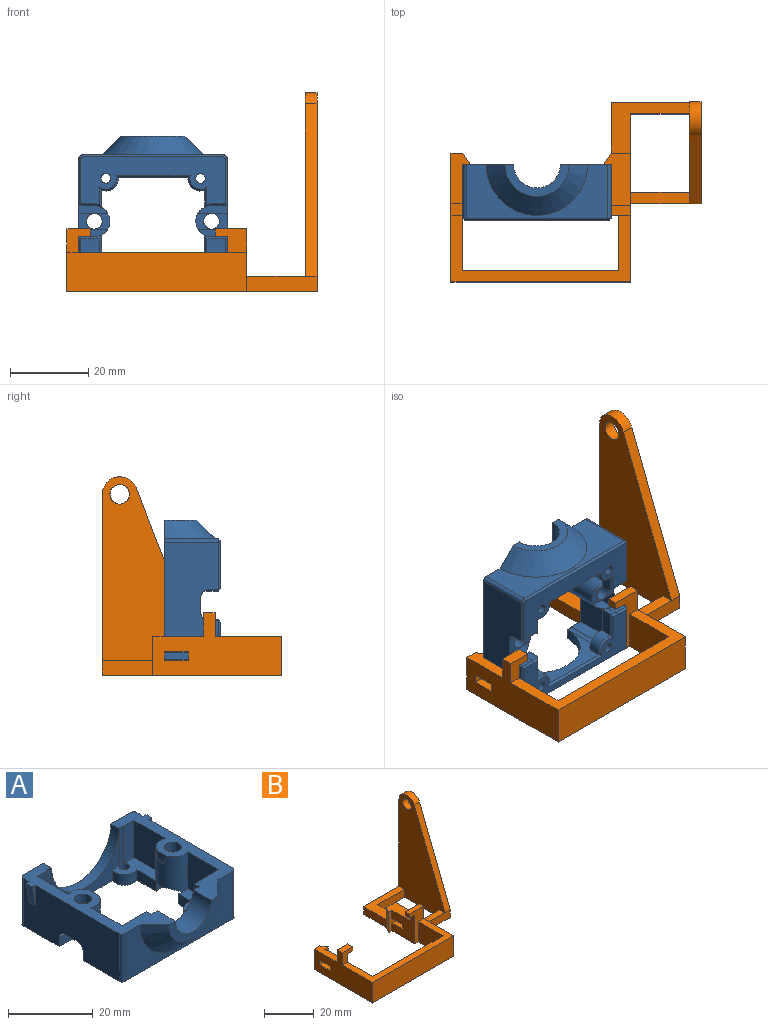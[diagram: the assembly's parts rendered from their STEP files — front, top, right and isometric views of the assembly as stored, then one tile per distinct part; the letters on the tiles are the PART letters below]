
ASSEMBLY  parts=2 mates=1
PART A: 100 faces, bbox 40.4x39.2x14.7 mm
  f0: cylinder r=2mm len=7.46mm, axis (1,0,0), area 18.6mm2, adj f8,f9,f10,f15,f16,f34,f89,f91
  f1: cylinder r=2mm len=7.46mm, axis (-1,0,0), area 18.6mm2, adj f4,f5,f11,f14,f17,f23,f86,f88
  f2: cylinder r=2mm len=7.46mm, axis (-1,0,0), area 18.6mm2, adj f7,f8,f10,f34,f36,f38,f89,f90
  f3: cylinder r=2mm len=7.46mm, axis (1,0,0), area 18.6mm2, adj f5,f6,f11,f23,f28,f32,f86,f87
  f4: cylinder r=4mm len=3mm, axis (0,0,-1), area 5.4mm2, adj f1,f14,f44,f88,f95
  f5: cylinder r=4mm len=10.75mm, axis (0,0,-1), area 143.3mm2, adj f1,f3,f14,f17,f27,f28,f32,f39
  f6: cylinder r=4mm len=3mm, axis (0,0,-1), area 5.4mm2, adj f3,f28,f45,f87,f93
  f7: cylinder r=4mm len=3mm, axis (0,0,-1), area 5.4mm2, adj f2,f38,f43,f90,f97
  f8: cylinder r=4mm len=10.75mm, axis (0,0,-1), area 143.3mm2, adj f0,f2,f10,f15,f16,f26,f36,f38
  f9: cylinder r=4mm len=3mm, axis (0,0,-1), area 5.4mm2, adj f0,f15,f42,f91,f99
  f10: plane 4x4mm, normal (0,0,-1), area 9mm2, adj f0,f2,f8,f19
  f11: plane 4x4mm, normal (0,0,-1), area 9.7mm2, adj f1,f3,f18,f23
  f12: plane 37.38x12.57mm, normal (0,0,-1), area 262.9mm2, adj f21,f51,f52,f53,f57,f58,f61,f63
  f13: plane 37.38x12.57mm, normal (0,0,-1), area 186.9mm2, adj f20,f54,f55,f56,f59,f60,f66,f68
  f14: plane 12.72x10.63mm, normal (0,0,1), area 67.5mm2, adj f1,f4,f5,f17,f29,f33,f41,f44
  f15: plane 10.63x7.24mm, normal (0,0,1), area 41.8mm2, adj f0,f8,f9,f16,f25,f31,f42,f67
  f16: plane 10.75x10.38mm, normal (1,0,0), area 111.6mm2, adj f0,f8,f15,f26,f31
  f17: plane 10.75x10.38mm, normal (-1,0,0), area 111.6mm2, adj f1,f5,f14,f27,f33
  f18: cylinder r=2mm len=9.25mm, axis (0,0,-1), area 116.2mm2, adj f11,f27,f86
  f19: cylinder r=2mm len=9.25mm, axis (0,0,-1), area 116.2mm2, adj f10,f26,f89
  f20: plane 12.28x0.52mm, normal (-0.71,0,-0.71), area 8.3mm2, adj f13,f34,f82,f83,f98
  f21: plane 12.28x0.52mm, normal (0.71,0,-0.71), area 8.3mm2, adj f12,f23,f80,f81,f94
  f22: plane 6x1mm, normal (0,1,0), area 3mm2, adj f23,f27,f73
  f23: plane 32x13.75mm, normal (1,0,0), area 393.7mm2, adj f1,f3,f11,f21,f22,f27,f59,f69
  f24: plane 10.75x3.35mm, normal (0,-1,0), area 36mm2, adj f27,f28,f32,f66
  f25: plane 22.63x13.75mm, normal (0,-1,0), area 96.8mm2, adj f15,f26,f28,f30,f56,f65,f66,f67
  f26: plane 38.8x14mm, normal (0,0,1), area 179mm2, adj f8,f16,f19,f25,f30,f31,f33,f34
  f27: plane 38.8x14mm, normal (0,0,1), area 179mm2, adj f5,f17,f18,f22,f23,f24,f30,f32
  f28: plane 10.63x7.41mm, normal (0,0,1), area 42.4mm2, adj f3,f5,f6,f24,f25,f32,f45,f65
  f29: cylinder r=11.3mm len=6.97mm, axis (0,1,0), area 21.2mm2, adj f14,f33,f38,f41
  f30: cylinder r=11.3mm len=22.6mm, axis (0,1,0), area 99.4mm2, adj f25,f26,f27,f37,f66
  f31: plane 10.75x3.18mm, normal (0,-1,0), area 34.2mm2, adj f15,f16,f26,f68
  f32: plane 10.75x10.38mm, normal (-1,0,0), area 111.6mm2, adj f3,f5,f24,f27,f28
  f33: plane 32.4x11.3mm, normal (0,1,0), area 250.3mm2, adj f14,f17,f26,f27,f29,f36,f38,f46
  f34: plane 32x13.75mm, normal (-1,0,0), area 393.7mm2, adj f0,f2,f20,f26,f58,f70,f71,f72
  f35: plane 36x13.75mm, normal (0,-1,0), area 229.5mm2, adj f26,f27,f50,f57,f78,f80
  f36: plane 10.75x10.38mm, normal (1,0,0), area 111.6mm2, adj f2,f8,f26,f33,f38
  f37: plane 36x13.75mm, normal (0,1,0), area 294.4mm2, adj f26,f27,f30,f60,f82,f84
  f38: plane 12.72x10.63mm, normal (0,0,1), area 68mm2, adj f2,f7,f8,f29,f33,f36,f41,f43
  f39: cylinder r=11.3mm len=3.04mm, axis (0,1,0), area 6.3mm2, adj f5,f27
  f40: cylinder r=11.3mm len=3.04mm, axis (0,1,0), area 6.3mm2, adj f8,f26
  f41: plane 17.76x3mm, normal (0,1,0), area 50.7mm2, adj f14,f29,f38,f51,f62,f64
  f42: plane 6.58x3mm, normal (1,0,0), area 19.7mm2, adj f9,f15,f55,f67
  f43: plane 4.39x3mm, normal (1,0,0), area 13.2mm2, adj f7,f38,f53,f62
  f44: plane 4.34x3mm, normal (-1,0,0), area 13mm2, adj f4,f14,f52,f64
  f45: plane 6.64x3mm, normal (-1,0,0), area 19.9mm2, adj f6,f28,f54,f65
  f46: cylinder r=8mm len=16mm, axis (0,1,0), area 40.2mm2, adj f26,f27,f33,f47
  f47: plane 16x8mm, normal (0,1,0), area 44mm2, adj f26,f27,f46,f48
  f48: cylinder r=6mm len=12mm, axis (0,1,0), area 113.1mm2, adj f26,f27,f47,f49
  f49: plane 16.4x8.2mm, normal (0,-1,0), area 49.1mm2, adj f26,f27,f48,f50
  f50: cone r=9mm half-angle=45deg, axis (0,1,0), area 226.1mm2, adj f26,f27,f35,f49
  f51: plane 18.98x0.54mm, normal (0,0.71,-0.71), area 13mm2, adj f12,f41,f74,f75
  f52: plane 5.19x0.57mm, normal (-0.71,0,-0.71), area 3.1mm2, adj f12,f44,f74,f95
  f53: plane 5.3x0.57mm, normal (0.71,0,-0.71), area 3.1mm2, adj f12,f43,f75,f97
  f54: plane 7.56x0.57mm, normal (-0.71,0,-0.71), area 4.7mm2, adj f13,f45,f77,f93
  f55: plane 7.43x0.56mm, normal (0.71,0,-0.71), area 4.6mm2, adj f13,f42,f76,f99
  f56: plane 19.64x0.56mm, normal (0,-0.71,-0.71), area 13.3mm2, adj f13,f25,f76,f77
  f57: plane 36.53x0.52mm, normal (0,-0.71,-0.71), area 25.5mm2, adj f12,f35,f78,f79,f80,f81
  f58: plane 12.28x0.52mm, normal (-0.71,0,-0.71), area 8.3mm2, adj f12,f34,f78,f79,f96
  f59: plane 12.28x0.52mm, normal (0.71,0,-0.71), area 8.3mm2, adj f13,f23,f84,f85,f92
  f60: plane 36.53x0.52mm, normal (0,0.71,-0.71), area 25.5mm2, adj f13,f37,f82,f83,f84,f85
  f61: cylinder r=1.25mm len=3.5mm, axis (0,0,-1), area 27.5mm2, adj f12,f38
  f62: cylinder r=3.25mm len=4.39mm, axis (0,0,-1), area 19.4mm2, adj f38,f41,f43,f75
  f63: cylinder r=1.25mm len=3.5mm, axis (0,0,-1), area 27.5mm2, adj f12,f14
  f64: cylinder r=3.25mm len=4.26mm, axis (0,0,-1), area 19mm2, adj f14,f41,f44,f74
  f65: cylinder r=3.25mm len=4.41mm, axis (0,0,-1), area 21.8mm2, adj f25,f28,f45,f77
  f66: cylinder r=1.25mm len=14.25mm, axis (0,0,-1), area 46.4mm2, adj f13,f24,f25,f27,f28,f30
  f67: cylinder r=3.25mm len=4.24mm, axis (0,0,-1), area 21.2mm2, adj f15,f25,f42,f76
  f68: cylinder r=1.25mm len=14.25mm, axis (0,0,-1), area 46.5mm2, adj f13,f15,f25,f26,f31
  f69: plane 6x1mm, normal (0,-1,0), area 3mm2, adj f23,f27,f73
  f70: plane 6x1mm, normal (0,-1,0), area 3mm2, adj f26,f34,f72
  f71: plane 6x1mm, normal (0,1,0), area 3mm2, adj f26,f34,f72
  f72: plane 6x2mm, normal (-0.99,0,-0.16), area 12.2mm2, adj f26,f34,f70,f71
  f73: plane 6x2mm, normal (0.99,0,-0.16), area 12.2mm2, adj f22,f23,f27,f69
  f74: cone r=2.75mm half-angle=45deg, axis (0,0,1), area 4.6mm2, adj f12,f51,f52,f64
  f75: cone r=2.75mm half-angle=45deg, axis (0,0,1), area 4.7mm2, adj f12,f51,f53,f62
  f76: cone r=2.75mm half-angle=45deg, axis (0,0,1), area 5.2mm2, adj f13,f55,f56,f67
  f77: cone r=2.75mm half-angle=45deg, axis (0,0,1), area 5.3mm2, adj f13,f54,f56,f65
  f78: cylinder r=1mm len=13.78mm, axis (0,0,-1), area 21.6mm2, adj f26,f34,f35,f57,f58,f79
  f79: cylinder r=1mm len=1.17mm, axis (-0.58,-0.58,0.58), area 0.8mm2, adj f12,f57,f58,f78
  f80: cylinder r=1mm len=13.78mm, axis (0,0,1), area 21.6mm2, adj f21,f23,f27,f35,f57,f81
  f81: cylinder r=1mm len=1.17mm, axis (0.58,-0.58,0.58), area 0.8mm2, adj f12,f21,f57,f80
  f82: cylinder r=1mm len=13.78mm, axis (0,0,1), area 21.6mm2, adj f20,f26,f34,f37,f60,f83
  f83: cylinder r=1mm len=1.17mm, axis (0.58,-0.58,-0.58), area 0.8mm2, adj f13,f20,f60,f82
  f84: cylinder r=1mm len=13.78mm, axis (0,0,-1), area 21.6mm2, adj f23,f27,f37,f59,f60,f85
  f85: cylinder r=1mm len=1.17mm, axis (-0.58,-0.58,-0.58), area 0.8mm2, adj f13,f59,f60,f84
  f86: plane 4x4mm, normal (0,0,-1), area 9mm2, adj f1,f3,f5,f18
  f87: plane 4x2.5mm, normal (0,-1,0), area 10mm2, adj f3,f6,f23,f92
  f88: plane 4x2.5mm, normal (0,1,0), area 10mm2, adj f1,f4,f23,f94
  f89: plane 4x4mm, normal (0,0,-1), area 9.7mm2, adj f0,f2,f19,f34
  f90: plane 4x2.5mm, normal (0,1,0), area 10mm2, adj f2,f7,f34,f96
  f91: plane 4x2.5mm, normal (0,-1,0), area 10mm2, adj f0,f9,f34,f98
  f92: plane 4x0.5mm, normal (0,-0.71,-0.71), area 2.7mm2, adj f13,f59,f87,f93
  f93: cone r=4mm half-angle=45deg, axis (0,0,-1), area 1.1mm2, adj f6,f13,f54,f92
  f94: plane 4x0.5mm, normal (0,0.71,-0.71), area 2.7mm2, adj f12,f21,f88,f95
  f95: cone r=4mm half-angle=45deg, axis (0,0,-1), area 1.1mm2, adj f4,f12,f52,f94
  f96: plane 4x0.5mm, normal (0,0.71,-0.71), area 2.7mm2, adj f12,f58,f90,f97
  f97: cone r=4mm half-angle=45deg, axis (0,0,-1), area 1.1mm2, adj f7,f12,f53,f96
  f98: plane 4x0.5mm, normal (0,-0.71,-0.71), area 2.7mm2, adj f13,f20,f91,f99
  f99: cone r=4mm half-angle=45deg, axis (0,0,-1), area 1.1mm2, adj f9,f13,f55,f98
PART B: 45 faces, bbox 64x46x50.8 mm
  f0: plane 50.8x26mm, normal (1,0,0), area 862mm2, adj f33,f37,f38,f42,f43,f44
  f1: plane 15x3mm, normal (0,0,1), area 45mm2, adj f3,f38,f40,f41
  f2: plane 6.2x5mm, normal (0,1,0), area 31mm2, adj f3,f23,f27,f36
  f3: plane 43x16mm, normal (1,0,0), area 358.4mm2, adj f1,f2,f6,f7,f9,f10,f19,f20
  f4: plane 3x2.5mm, normal (0,0,-1), area 7.5mm2, adj f5,f7,f8,f9
  f5: plane 2.5x2mm, normal (-1,0,0), area 5mm2, adj f4,f6,f7,f9
  f6: plane 8x2.5mm, normal (0,0,1), area 20mm2, adj f3,f5,f7,f9
  f7: plane 16x8mm, normal (0,-1,0), area 56mm2, adj f3,f4,f5,f6,f8,f10,f33,f34
  f8: plane 14x12.91mm, normal (-1,0,0), area 125.9mm2, adj f4,f7,f9,f20,f21,f22,f23,f28
  f9: plane 8x6mm, normal (0,1,0), area 36mm2, adj f3,f4,f5,f6,f8,f23
  f10: plane 46x17.09mm, normal (0,0,1), area 222.5mm2, adj f3,f7,f14,f15,f16,f19,f32,f34
  f11: plane 3x2mm, normal (1,0,0), area 6mm2, adj f12,f13,f15,f17
  f12: plane 3x3mm, normal (0,0,-1), area 9mm2, adj f11,f15,f16,f17
  f13: plane 6x3mm, normal (0,0,1), area 18mm2, adj f11,f14,f15,f17
  f14: plane 33x16mm, normal (-1,0,0), area 334.8mm2, adj f10,f13,f15,f17,f18,f19,f24,f25
  f15: plane 6x6mm, normal (0,-1,0), area 24mm2, adj f10,f11,f12,f13,f14,f16
  f16: plane 27x14mm, normal (1,0,0), area 268.8mm2, adj f10,f12,f15,f17,f18,f24,f25,f26
  f17: plane 6x6mm, normal (0,1,0), area 24mm2, adj f11,f12,f13,f14,f16,f18
  f18: plane 12.91x5mm, normal (0,0,1), area 41.7mm2, adj f14,f16,f17,f29,f30,f31
  f19: plane 46x10mm, normal (0,-1,0), area 460mm2, adj f3,f10,f14,f33
  f20: plane 6x5mm, normal (0,0,1), area 30mm2, adj f3,f8,f22,f28
  f21: plane 6x5mm, normal (0,0,-1), area 30mm2, adj f3,f8,f22,f28
  f22: plane 5x2.2mm, normal (0,1,0), area 11mm2, adj f3,f8,f20,f21
  f23: plane 13.41x7mm, normal (0,0,1), area 70.1mm2, adj f2,f3,f8,f9,f27,f28
  f24: plane 6x3mm, normal (0,0,1), area 18mm2, adj f14,f16,f25,f29
  f25: plane 3x2.2mm, normal (0,1,0), area 6.6mm2, adj f14,f16,f24,f26
  f26: plane 6x3mm, normal (0,0,-1), area 18mm2, adj f14,f16,f25,f29
  f27: plane 10x3mm, normal (-0.83,0.55,0), area 36.1mm2, adj f2,f23,f28,f33,f35
  f28: plane 10x7mm, normal (0,-1,0), area 31mm2, adj f3,f8,f20,f21,f23,f27,f33
  f29: plane 10x5mm, normal (0,-1,0), area 26.6mm2, adj f14,f16,f18,f24,f26,f30,f33
  f30: plane 10x3mm, normal (0.83,0.55,0), area 36.1mm2, adj f18,f29,f31,f33
  f31: plane 10x3mm, normal (0,1,0), area 30mm2, adj f14,f18,f30,f33
  f32: plane 40x10mm, normal (0,1,0), area 400mm2, adj f10,f16,f33,f34
  f33: plane 64x46mm, normal (0,0,-1), area 588.8mm2, adj f0,f3,f7,f8,f14,f16,f19,f27
  f34: plane 14.09x10mm, normal (-1,0,0), area 140.9mm2, adj f7,f10,f32,f33
  f35: plane 13x3.8mm, normal (-1,0,0), area 49.4mm2, adj f27,f33,f36,f37
  f36: plane 20x13mm, normal (0,0,1), area 110mm2, adj f2,f3,f35,f37,f39,f40
  f37: plane 46.3x23mm, normal (0,1,0), area 214.9mm2, adj f0,f33,f35,f36,f40,f43
  f38: plane 18x3.8mm, normal (0,-1,0), area 68.4mm2, adj f0,f1,f3,f33,f42
  f39: plane 15x3.8mm, normal (0,-1,0), area 57mm2, adj f3,f33,f36,f40
  f40: plane 50.8x26mm, normal (-1,0,0), area 839.2mm2, adj f1,f33,f36,f37,f39,f41,f42,f43
  f41: plane 15x3.8mm, normal (0,1,0), area 57mm2, adj f1,f3,f33,f40
  f42: plane 44.14x17.31mm, normal (0,-0.93,0.37), area 142.2mm2, adj f0,f38,f40,f43
  f43: cylinder r=4.5mm len=8.69mm, axis (-1,0,0), area 37.4mm2, adj f0,f37,f40,f42
  f44: cylinder r=2.5mm len=5mm, axis (-1,0,0), area 47.1mm2, adj f0,f40
PLACE A rot(axis=(-1,0,0),90deg) t=(0,12.07,12.02)mm
PLACE B t=(0,25.82,-5.88)mm
MATE fastened B.f8 <-> A.f23  axis (-1,0,0) through (19,16.82,-0.98)mm
